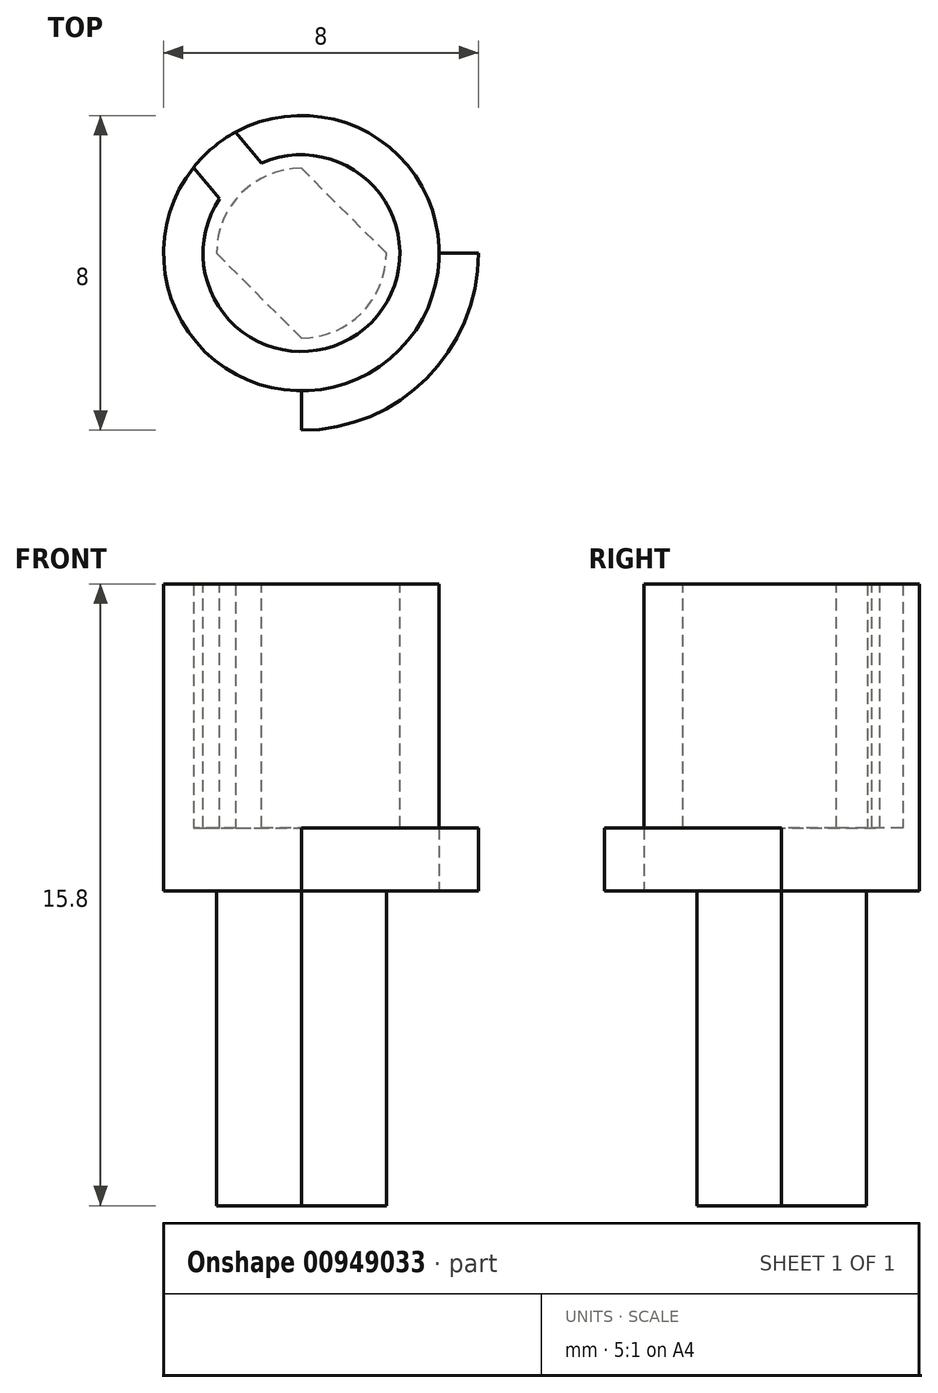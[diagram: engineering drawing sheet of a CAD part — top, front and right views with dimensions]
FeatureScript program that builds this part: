
annotation { "Feature Type Name" : "Feature", "Feature Type Description" : "" }
export const myFeature = defineFeature(function(context is Context, id is Id, definition is map)
    precondition{}
    {
        {
            var Q0;
            Q0=qCreatedBy(makeId("Top.planeOp"),FACE);
            var sketch = newSketch(context, id + "F0", { "sketchPlane" : qUnion([Q0])});
            skCircle(sketch, "E0", {"center": v(0, 0) * mm, "radius": 3.5 * mm});
            skCircle(sketch, "E1", {"center": v(0, 0) * mm, "radius": 4.5 * mm});
            skLineSegment(sketch, "E2", {"start": v(0, 0) * mm, "end": v(0, -4.5) * mm});
            skLineSegment(sketch, "E3", {"start": v(0, 0) * mm, "end": v(4.5, 0) * mm});
            skLineSegment(sketch, "E4", {"start": v(0, 0) * mm, "end": v(-2.9, 3.45) * mm, "construction": true});
            skLineSegment(sketch, "E5", {"start": v(-2.9, 3.45) * mm, "end": v(-2.36, 3.9) * mm});
            skLineSegment(sketch, "E6.MirrorCS", {"start": v(-2.9, 3.45) * mm, "end": v(-3.43, 3) * mm});
            skLineSegment(sketch, "E7", {"start": v(-2.36, 3.9) * mm, "end": v(-0.7, 1.93) * mm});
            skLineSegment(sketch, "E8", {"start": v(-0.7, 1.93) * mm, "end": v(-1.24, 1.48) * mm});
            skLineSegment(sketch, "E9.MirrorCS", {"start": v(-3.43, 3) * mm, "end": v(-1.78, 1.03) * mm});
            skLineSegment(sketch, "E10.MirrorCS", {"start": v(-1.78, 1.03) * mm, "end": v(-1.24, 1.48) * mm});
            skSolve(sketch);
        }
        {
            var Q0;
            {var subQ0=sQuery(id+"F0.wireOp",EDGE,"E2");var subQ1=sQuery(id+"F0.wireOp",EDGE,"E0");var subQ2=makeQuery(id+"F0.imprint","INTERSECT",VERTEX,{"derivedFrom":[subQ1,subQ0]});Q0=makeQuery(id+"F0.imprint","IMPRINT",FACE,{"disambiguationData":[TD([[makeQuery(id+"F0.imprint","IMPRINT",EDGE,{"disambiguationData":[TD([[subQ2,-1.0]])],"derivedFrom":subQ1}),1.0]])]});}
            var Q1;
            {var subQ0=sQuery(id+"F0.wireOp",EDGE,"E2");var subQ1=sQuery(id+"F0.wireOp",EDGE,"E0");var subQ2=makeQuery(id+"F0.imprint","INTERSECT",VERTEX,{"derivedFrom":[subQ1,subQ0]});Q1=makeQuery(id+"F0.imprint","IMPRINT",FACE,{"disambiguationData":[TD([[makeQuery(id+"F0.imprint","IMPRINT",EDGE,{"disambiguationData":[TD([[subQ2,1.0]])],"derivedFrom":subQ1}),1.0]])]});}
            extrude(context, id + "F1", {"entities" : qUnion([Q0, Q1]), "depth" : 7.8 * mm, "offsetDistance" : 25 * mm});
        }
        {
            var Q0;
            Q0=makeQuery(id+"F1.opExtrude","CAP_FACE",FACE,{"disambiguationData":[OSD([sQuery(id+"F0.wireOp",EDGE,"E0"),sQuery(id+"F0.wireOp",EDGE,"E7"),sQuery(id+"F0.wireOp",EDGE,"E8"),sQuery(id+"F0.wireOp",EDGE,"E9.MirrorCS"),sQuery(id+"F0.wireOp",EDGE,"E10.MirrorCS")])],"isStart":false});
            var sketch = newSketch(context, id + "F2", { "sketchPlane" : qUnion([Q0])});
            skCircle(sketch, "E11", {"center": v(0, 0) * mm, "radius": 2.5 * mm});
            skSolve(sketch);
        }
        {
            var Q0;
            {var subQ5=makeQuery(id+"F1.opExtrude","CAP_EDGE",EDGE,{"disambiguationData":[OSD([sQuery(id+"F0.wireOp",EDGE,"E8"),sQuery(id+"F0.wireOp",EDGE,"E10.MirrorCS")])],"isStart":false});Q0=makeQuery(id+"F2.imprint","IMPRINT",FACE,{"disambiguationData":[TD([[makeQuery(id+"F2.imprint","IMPRINT",EDGE,{"derivedFrom":subQ5}),1.0]])]});}
            extrude(context, id + "F3", {"entities" : qUnion([Q0]), "operationType" : NewBodyOperationType.REMOVE, "oppositeDirection" : true, "depth" : 6.2 * mm, "offsetDistance" : 25 * mm});
        }
        {
            var Q0;
            {var subQ0=sQuery(id+"F0.wireOp",EDGE,"E8");Q0=makeQuery(id+"F0.imprint","IMPRINT",FACE,{"disambiguationData":[TD([[makeQuery(id+"F0.imprint","IMPRINT",EDGE,{"derivedFrom":subQ0}),-1.0]])]});}
            var Q1;
            {var subQ0=sQuery(id+"F0.wireOp",EDGE,"E3");var subQ1=sQuery(id+"F0.wireOp",EDGE,"E0");var subQ2=makeQuery(id+"F0.imprint","INTERSECT",VERTEX,{"derivedFrom":[subQ1,subQ0]});Q1=makeQuery(id+"F0.imprint","IMPRINT",FACE,{"disambiguationData":[TD([[makeQuery(id+"F0.imprint","IMPRINT",EDGE,{"disambiguationData":[TD([[subQ2,1.0]])],"derivedFrom":subQ1}),-1.0]])]});}
            extrude(context, id + "F4", {"entities" : qUnion([Q0, Q1]), "operationType" : NewBodyOperationType.ADD, "depth" : 1.6 * mm, "offsetDistance" : 25 * mm});
        }
        {
            var Q0;
            {var subQ0=sQuery(id+"F0.wireOp",EDGE,"E0");var subQ1=sQuery(id+"F0.wireOp",EDGE,"E10.MirrorCS");var subQ2=sQuery(id+"F0.wireOp",EDGE,"E9.MirrorCS");var subQ3=sQuery(id+"F0.wireOp",EDGE,"E8");var subQ4=sQuery(id+"F0.wireOp",EDGE,"E7");Q0=makeQuery(id+"F4.boolean.opBoolean","MERGE",FACE,{"derivedFrom":[makeQuery(id+"F1.opExtrude","CAP_FACE",FACE,{"disambiguationData":[OSD([subQ0,subQ4,subQ3,subQ2,subQ1])],"isStart":true}),makeQuery(id+"F4.opExtrude","CAP_FACE",FACE,{"disambiguationData":[OSD([subQ0,subQ4,subQ3,subQ2,subQ1])],"isStart":true}),makeQuery(id+"F4.opExtrude","CAP_FACE",FACE,{"disambiguationData":[OSD([subQ0,sQuery(id+"F0.wireOp",EDGE,"E2"),sQuery(id+"F0.wireOp",EDGE,"E3"),sQuery(id+"F0.wireOp",EDGE,"E1")])],"isStart":true})]});}
            var sketch = newSketch(context, id + "F5", { "sketchPlane" : qUnion([Q0])});
            skLineSegment(sketch, "E12", {"start": v(0, 0) * mm, "end": v(0, -3.5) * mm, "construction": true});
            skLineSegment(sketch, "E13", {"start": v(0, 0) * mm, "end": v(-2.47, -2.47) * mm, "construction": true});
            skCircle(sketch, "E14.cCircle", {"center": v(0, 0) * mm, "radius": 1.52 * mm, "construction": true});
            skLineSegment(sketch, "E14.0", {"start": v(0, -2.16) * mm, "end": v(-2.16, 0) * mm});
            skLineSegment(sketch, "E14.1", {"start": v(-2.16, 0) * mm, "end": v(0, 2.16) * mm});
            skLineSegment(sketch, "E14.2", {"start": v(0, 2.16) * mm, "end": v(2.16, 0) * mm});
            skLineSegment(sketch, "E14.3", {"start": v(2.16, 0) * mm, "end": v(0, -2.16) * mm});
            skPoint(sketch, "E14.0.midPoint", {"position": v(-1.08, -1.08) * mm});
            skSolve(sketch);
        }
        {
            var Q0;
            Q0=makeQuery(id+"F5.imprint","IMPRINT",FACE,{"disambiguationData":[TD([[makeQuery(id+"F5.imprint","IMPRINT",EDGE,{"derivedFrom":sQuery(id+"F5.wireOp",EDGE,"E14.0")}),-1.0]])]});
            extrude(context, id + "F6", {"entities" : qUnion([Q0]), "operationType" : NewBodyOperationType.ADD, "depth" : 8 * mm, "offsetDistance" : 25 * mm});
        }
        {
            var Q0;
            Q0=makeQuery(id+"F6.opExtrude","CAP_FACE",FACE,{"disambiguationData":[OSD([sQuery(id+"F5.wireOp",EDGE,"E14.0"),sQuery(id+"F5.wireOp",EDGE,"E14.1"),sQuery(id+"F5.wireOp",EDGE,"E14.2"),sQuery(id+"F5.wireOp",EDGE,"E14.3")])],"isStart":false});
            var sketch = newSketch(context, id + "F7", { "sketchPlane" : qUnion([Q0])});
            skArc(sketch, "E15", {"start": v(-2.16, 0) * mm, "mid": v(-1.52, -1.52) * mm, "end": v(0, -2.16) * mm});
            skPoint(sketch, "E16", {"position": v(-2.16, 0) * mm});
            skPoint(sketch, "E17", {"position": v(0, 2.16) * mm});
            skPoint(sketch, "E18", {"position": v(2.16, 0) * mm});
            skPoint(sketch, "E19", {"position": v(0, -2.16) * mm});
            skArc(sketch, "E20.trimOffspring", {"start": v(2.16, 0) * mm, "mid": v(1.52, 1.52) * mm, "end": v(0, 2.16) * mm});
            skSolve(sketch);
        }
        {
            var Q0;
            Q0=makeQuery(id+"F7.imprint","IMPRINT",FACE,{"disambiguationData":[TD([[makeQuery(id+"F7.imprint","IMPRINT",EDGE,{"derivedFrom":sQuery(id+"F7.wireOp",EDGE,"E15")}),1.0]])]});
            var Q1;
            Q1=makeQuery(id+"F7.imprint","IMPRINT",FACE,{"disambiguationData":[TD([[makeQuery(id+"F7.imprint","IMPRINT",EDGE,{"derivedFrom":sQuery(id+"F7.wireOp",EDGE,"E20.trimOffspring")}),1.0]])]});
            extrude(context, id + "F8", {"entities" : qUnion([Q0, Q1]), "operationType" : NewBodyOperationType.ADD, "oppositeDirection" : true, "depth" : 8.7 * mm, "offsetDistance" : 25 * mm});
        }
    });
